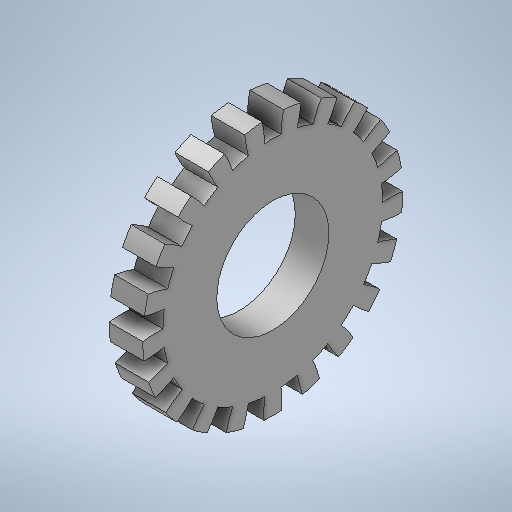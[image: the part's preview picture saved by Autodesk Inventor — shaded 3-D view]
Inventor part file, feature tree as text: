
AUTODESK INVENTOR PART (.ipt)
format: ipt  version: 2025.2 (Build 292293000, 293)  size: 376,320 bytes
history: native  units: in
note: dims shown in document units (in); Inventor stores cm internally (conversion verified against a paired STEP export)
features: other x4, extrude x1, pattern_circular x1
ambient origin geometry x8: Origin, YZ Plane, XZ Plane, XY Plane, X Axis, Y Axis, Z Axis, Center Point
bodies: Volumenkörper1 (feature_tree)
feature tree (6):
  other  "Skelett_Laufkatze.ipt"
  other  "Zahnrad_Rohling"
  extrude  "Zahngeometrie"  Depth=0.3937in
  pattern_circular  "Anzahl_zähne"  Angle=90.0deg  [1 undecoded]
  other  "Zahnrad_Laufrad_seite"
  other  "Zahnrad_Laufrad_front"
note: 1 required parameter value undecoded (feature->parameter linkage not recoverable at this tier; creation-order binding heuristic only, values carry confidence <= 0.55)
